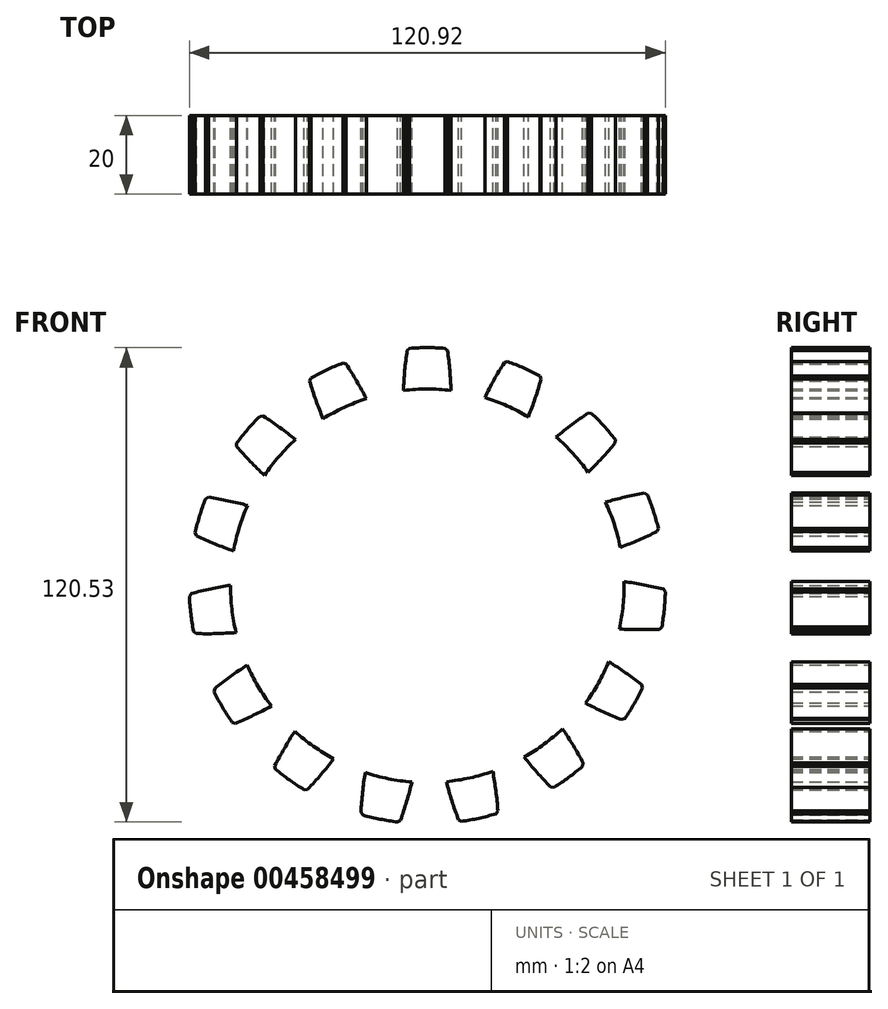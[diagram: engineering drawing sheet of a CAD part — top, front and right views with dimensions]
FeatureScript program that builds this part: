
annotation { "Feature Type Name" : "Feature", "Feature Type Description" : "" }
export const myFeature = defineFeature(function(context is Context, id is Id, definition is map)
    precondition{}
    {
        {
            var Q0;
            Q0=qCreatedBy(makeId("Front.planeOp"),FACE);
            var sketch = newSketch(context, id + "F0", { "sketchPlane" : qUnion([Q0])});
            skCircle(sketch, "E0", {"center": v(0, 0) * mm, "radius": 50 * mm});
            skArc(sketch, "E1", {"start": v(-2.05, -12.38) * mm, "mid": v(0, -12.55) * mm, "end": v(2.05, -12.38) * mm});
            skLineSegment(sketch, "E2.right", {"start": v(2.05, 10.3) * mm, "end": v(2.05, -12.38) * mm});
            skLineSegment(sketch, "E3.right", {"start": v(-2.05, 10.5) * mm, "end": v(-2.05, -12.38) * mm});
            skLineSegment(sketch, "E4", {"start": v(2.05, 10.3) * mm, "end": v(2.05, 12.38) * mm});
            skLineSegment(sketch, "E5", {"start": v(2.05, 12.38) * mm, "end": v(2.05, 10.3) * mm});
            skLineSegment(sketch, "E6", {"start": v(-2.05, 10.5) * mm, "end": v(-2.05, 12.38) * mm});
            skPoint(sketch, "E7.orphan", {"position": v(0, 10.5) * mm});
            skArc(sketch, "E8.trimOffspring", {"start": v(2.05, 12.38) * mm, "mid": v(0, 12.55) * mm, "end": v(-2.05, 12.38) * mm});
            skLineSegment(sketch, "E9.1.0", {"start": v(-7.83, 7.29) * mm, "end": v(5.62, -11.22) * mm});
            skLineSegment(sketch, "E9.1.1", {"start": v(-7.83, 7.29) * mm, "end": v(-8.94, 8.81) * mm});
            skArc(sketch, "E9.1.2", {"start": v(-5.62, 11.22) * mm, "mid": v(-7.38, 10.15) * mm, "end": v(-8.94, 8.81) * mm});
            skLineSegment(sketch, "E9.1.3", {"start": v(-4.4, 9.54) * mm, "end": v(8.94, -8.81) * mm});
            skLineSegment(sketch, "E9.1.4", {"start": v(-5.62, 11.22) * mm, "end": v(-4.4, 9.54) * mm});
            skArc(sketch, "E9.1.5", {"start": v(5.62, -11.22) * mm, "mid": v(7.38, -10.15) * mm, "end": v(8.94, -8.81) * mm});
            skLineSegment(sketch, "E9.2.0", {"start": v(-10.62, 1.3) * mm, "end": v(11.14, -5.78) * mm});
            skLineSegment(sketch, "E9.2.1", {"start": v(-10.62, 1.3) * mm, "end": v(-12.4, 1.88) * mm});
            skArc(sketch, "E9.2.2", {"start": v(-11.14, 5.78) * mm, "mid": v(-11.94, 3.88) * mm, "end": v(-12.4, 1.88) * mm});
            skLineSegment(sketch, "E9.2.3", {"start": v(-9.16, 5.13) * mm, "end": v(12.4, -1.88) * mm});
            skLineSegment(sketch, "E9.2.4", {"start": v(-11.14, 5.78) * mm, "end": v(-9.16, 5.13) * mm});
            skArc(sketch, "E9.2.5", {"start": v(11.14, -5.78) * mm, "mid": v(11.94, -3.88) * mm, "end": v(12.4, -1.88) * mm});
            skLineSegment(sketch, "E9.3.0", {"start": v(-9.35, -5.2) * mm, "end": v(12.4, 1.88) * mm});
            skLineSegment(sketch, "E9.3.1", {"start": v(-9.35, -5.2) * mm, "end": v(-11.14, -5.78) * mm});
            skArc(sketch, "E9.3.2", {"start": v(-12.4, -1.88) * mm, "mid": v(-11.94, -3.88) * mm, "end": v(-11.14, -5.78) * mm});
            skLineSegment(sketch, "E9.3.3", {"start": v(-10.43, -1.23) * mm, "end": v(11.14, 5.78) * mm});
            skLineSegment(sketch, "E9.3.4", {"start": v(-12.4, -1.88) * mm, "end": v(-10.43, -1.23) * mm});
            skArc(sketch, "E9.3.5", {"start": v(12.4, 1.88) * mm, "mid": v(11.94, 3.88) * mm, "end": v(11.14, 5.78) * mm});
            skLineSegment(sketch, "E9.4.0", {"start": v(-4.51, -9.7) * mm, "end": v(8.94, 8.81) * mm});
            skLineSegment(sketch, "E9.4.1", {"start": v(-4.51, -9.7) * mm, "end": v(-5.62, -11.22) * mm});
            skArc(sketch, "E9.4.2", {"start": v(-8.94, -8.81) * mm, "mid": v(-7.38, -10.15) * mm, "end": v(-5.62, -11.22) * mm});
            skLineSegment(sketch, "E9.4.3", {"start": v(-7.71, -7.13) * mm, "end": v(5.62, 11.22) * mm});
            skLineSegment(sketch, "E9.4.4", {"start": v(-8.94, -8.81) * mm, "end": v(-7.71, -7.13) * mm});
            skArc(sketch, "E9.4.5", {"start": v(8.94, 8.81) * mm, "mid": v(7.38, 10.15) * mm, "end": v(5.62, 11.22) * mm});
            skLineSegment(sketch, "E9.5.0", {"start": v(2.05, -10.5) * mm, "end": v(2.05, 12.38) * mm});
            skLineSegment(sketch, "E9.5.1", {"start": v(2.05, -10.5) * mm, "end": v(2.05, -12.38) * mm});
            skLineSegment(sketch, "E9.5.3", {"start": v(-2.05, -10.3) * mm, "end": v(-2.05, 12.38) * mm});
            skLineSegment(sketch, "E9.5.4", {"start": v(-2.05, -12.38) * mm, "end": v(-2.05, -10.3) * mm});
            skLineSegment(sketch, "E9.6.0", {"start": v(7.83, -7.29) * mm, "end": v(-5.62, 11.22) * mm});
            skLineSegment(sketch, "E9.6.1", {"start": v(7.83, -7.29) * mm, "end": v(8.94, -8.81) * mm});
            skArc(sketch, "E9.6.2", {"start": v(5.62, -11.22) * mm, "mid": v(7.38, -10.15) * mm, "end": v(8.94, -8.81) * mm});
            skLineSegment(sketch, "E9.6.3", {"start": v(4.4, -9.54) * mm, "end": v(-8.94, 8.81) * mm});
            skLineSegment(sketch, "E9.6.4", {"start": v(5.62, -11.22) * mm, "end": v(4.4, -9.54) * mm});
            skArc(sketch, "E9.6.5", {"start": v(-5.62, 11.22) * mm, "mid": v(-7.38, 10.15) * mm, "end": v(-8.94, 8.81) * mm});
            skLineSegment(sketch, "E9.7.0", {"start": v(10.62, -1.3) * mm, "end": v(-11.14, 5.78) * mm});
            skLineSegment(sketch, "E9.7.1", {"start": v(10.62, -1.3) * mm, "end": v(12.4, -1.88) * mm});
            skArc(sketch, "E9.7.2", {"start": v(11.14, -5.78) * mm, "mid": v(11.94, -3.88) * mm, "end": v(12.4, -1.88) * mm});
            skLineSegment(sketch, "E9.7.3", {"start": v(9.16, -5.13) * mm, "end": v(-12.4, 1.88) * mm});
            skLineSegment(sketch, "E9.7.4", {"start": v(11.14, -5.78) * mm, "end": v(9.16, -5.13) * mm});
            skArc(sketch, "E9.7.5", {"start": v(-11.14, 5.78) * mm, "mid": v(-11.94, 3.88) * mm, "end": v(-12.4, 1.88) * mm});
            skLineSegment(sketch, "E9.8.0", {"start": v(9.35, 5.2) * mm, "end": v(-12.4, -1.88) * mm});
            skLineSegment(sketch, "E9.8.1", {"start": v(9.35, 5.2) * mm, "end": v(11.14, 5.78) * mm});
            skArc(sketch, "E9.8.2", {"start": v(12.4, 1.88) * mm, "mid": v(11.94, 3.88) * mm, "end": v(11.14, 5.78) * mm});
            skLineSegment(sketch, "E9.8.3", {"start": v(10.43, 1.23) * mm, "end": v(-11.14, -5.78) * mm});
            skLineSegment(sketch, "E9.8.4", {"start": v(12.4, 1.88) * mm, "end": v(10.43, 1.23) * mm});
            skArc(sketch, "E9.8.5", {"start": v(-12.4, -1.88) * mm, "mid": v(-11.94, -3.88) * mm, "end": v(-11.14, -5.78) * mm});
            skLineSegment(sketch, "E9.9.0", {"start": v(4.51, 9.7) * mm, "end": v(-8.94, -8.81) * mm});
            skLineSegment(sketch, "E9.9.1", {"start": v(4.51, 9.7) * mm, "end": v(5.62, 11.22) * mm});
            skArc(sketch, "E9.9.2", {"start": v(8.94, 8.81) * mm, "mid": v(7.38, 10.15) * mm, "end": v(5.62, 11.22) * mm});
            skLineSegment(sketch, "E9.9.3", {"start": v(7.71, 7.13) * mm, "end": v(-5.62, -11.22) * mm});
            skLineSegment(sketch, "E9.9.4", {"start": v(8.94, 8.81) * mm, "end": v(7.71, 7.13) * mm});
            skArc(sketch, "E9.9.5", {"start": v(-8.94, -8.81) * mm, "mid": v(-7.38, -10.15) * mm, "end": v(-5.62, -11.22) * mm});
            skLineSegment(sketch, "E10", {"start": v(0, 50) * mm, "end": v(0, 46.5) * mm, "construction": true});
            skLineSegment(sketch, "E11", {"start": v(0, 46.5) * mm, "end": v(83.9, 46.5) * mm, "construction": true});
            skArc(sketch, "E12", {"start": v(-5.04, 60.29) * mm, "mid": v(-5.7, 54.98) * mm, "end": v(-6.05, 49.63) * mm});
            skArc(sketch, "E13", {"start": v(5.04, 60.29) * mm, "mid": v(0, 60.5) * mm, "end": v(-5.04, 60.29) * mm});
            skArc(sketch, "E14.MirrorC", {"start": v(5.04, 60.29) * mm, "mid": v(5.83, 53.42) * mm, "end": v(6.1, 46.5) * mm});
            skArc(sketch, "E15.trimOffspring", {"start": v(-6.8, 0.06) * mm, "mid": v(-6.85, -0.01) * mm, "end": v(-6.9, -0.08) * mm});
            skArc(sketch, "E16.trimOffspring", {"start": v(4.73, 3.7) * mm, "mid": v(4.84, 3.5) * mm, "end": v(4.94, 3.31) * mm});
            skArc(sketch, "E17.trimOffspring", {"start": v(6.8, 0.06) * mm, "mid": v(6.85, -0.01) * mm, "end": v(6.9, -0.08) * mm});
            skArc(sketch, "E18.1.0", {"start": v(29.06, 53.07) * mm, "mid": v(24.54, 55.3) * mm, "end": v(19.85, 57.15) * mm});
            skArc(sketch, "E18.1.1", {"start": v(19.85, 57.15) * mm, "mid": v(17.09, 52.56) * mm, "end": v(14.6, 47.82) * mm});
            skArc(sketch, "E18.1.2", {"start": v(29.06, 53.07) * mm, "mid": v(27, 46.46) * mm, "end": v(24.44, 40.03) * mm});
            skArc(sketch, "E18.2.0", {"start": v(48.08, 36.72) * mm, "mid": v(44.86, 40.6) * mm, "end": v(41.32, 44.19) * mm});
            skArc(sketch, "E18.2.1", {"start": v(41.32, 44.19) * mm, "mid": v(36.94, 41.11) * mm, "end": v(32.75, 37.79) * mm});
            skArc(sketch, "E18.2.2", {"start": v(48.08, 36.72) * mm, "mid": v(43.52, 31.52) * mm, "end": v(38.57, 26.68) * mm});
            skArc(sketch, "E18.3.0", {"start": v(58.84, 14.06) * mm, "mid": v(57.47, 18.91) * mm, "end": v(55.7, 23.63) * mm});
            skArc(sketch, "E18.3.1", {"start": v(55.7, 23.63) * mm, "mid": v(50.44, 22.6) * mm, "end": v(45.26, 21.26) * mm});
            skArc(sketch, "E18.3.2", {"start": v(58.84, 14.06) * mm, "mid": v(52.56, 11.15) * mm, "end": v(46.08, 8.74) * mm});
            skArc(sketch, "E18.4.0", {"start": v(59.49, -11.02) * mm, "mid": v(60.2, -6.02) * mm, "end": v(60.5, -1) * mm});
            skArc(sketch, "E18.4.1", {"start": v(60.5, -1) * mm, "mid": v(55.27, 0.2) * mm, "end": v(49.99, 1.07) * mm});
            skArc(sketch, "E18.4.2", {"start": v(59.49, -11.02) * mm, "mid": v(52.57, -11.12) * mm, "end": v(45.66, -10.7) * mm});
            skArc(sketch, "E18.5.0", {"start": v(49.9, -34.2) * mm, "mid": v(52.58, -29.92) * mm, "end": v(54.9, -25.44) * mm});
            skArc(sketch, "E18.5.1", {"start": v(54.9, -25.44) * mm, "mid": v(50.6, -22.24) * mm, "end": v(46.13, -19.3) * mm});
            skArc(sketch, "E18.5.2", {"start": v(49.9, -34.2) * mm, "mid": v(43.54, -31.49) * mm, "end": v(37.4, -28.3) * mm});
            skArc(sketch, "E18.6.0", {"start": v(31.75, -51.5) * mm, "mid": v(35.93, -48.68) * mm, "end": v(39.85, -45.52) * mm});
            skArc(sketch, "E18.6.1", {"start": v(39.85, -45.52) * mm, "mid": v(37.23, -40.85) * mm, "end": v(34.34, -36.34) * mm});
            skArc(sketch, "E18.6.2", {"start": v(31.75, -51.5) * mm, "mid": v(27.03, -46.44) * mm, "end": v(22.7, -41.04) * mm});
            skArc(sketch, "E18.7.0", {"start": v(8.13, -59.95) * mm, "mid": v(13.1, -59.07) * mm, "end": v(17.97, -57.77) * mm});
            skArc(sketch, "E18.7.1", {"start": v(17.97, -57.77) * mm, "mid": v(17.46, -52.44) * mm, "end": v(16.64, -47.15) * mm});
            skArc(sketch, "E18.7.2", {"start": v(8.13, -59.95) * mm, "mid": v(5.87, -53.41) * mm, "end": v(4.1, -46.72) * mm});
            skArc(sketch, "E18.8.0", {"start": v(-16.88, -58.1) * mm, "mid": v(-11.99, -59.3) * mm, "end": v(-7, -60.1) * mm});
            skArc(sketch, "E18.8.1", {"start": v(-7, -60.1) * mm, "mid": v(-5.3, -55.02) * mm, "end": v(-3.9, -49.85) * mm});
            skArc(sketch, "E18.8.2", {"start": v(-16.88, -58.1) * mm, "mid": v(-16.3, -51.2) * mm, "end": v(-15.2, -44.37) * mm});
            skArc(sketch, "E18.9.0", {"start": v(-39, -46.26) * mm, "mid": v(-35, -49.34) * mm, "end": v(-30.78, -52.09) * mm});
            skArc(sketch, "E18.9.1", {"start": v(-30.78, -52.09) * mm, "mid": v(-27.16, -48.14) * mm, "end": v(-23.8, -43.98) * mm});
            skArc(sketch, "E18.9.2", {"start": v(-39, -46.26) * mm, "mid": v(-35.67, -40.19) * mm, "end": v(-31.88, -34.4) * mm});
            skArc(sketch, "E18.10.0", {"start": v(-54.4, -26.46) * mm, "mid": v(-52.01, -30.9) * mm, "end": v(-49.26, -35.12) * mm});
            skArc(sketch, "E18.10.1", {"start": v(-49.26, -35.12) * mm, "mid": v(-44.35, -32.98) * mm, "end": v(-39.58, -30.55) * mm});
            skArc(sketch, "E18.10.2", {"start": v(-54.4, -26.46) * mm, "mid": v(-48.9, -22.27) * mm, "end": v(-43.1, -18.5) * mm});
            skArc(sketch, "E18.11.0", {"start": v(-60.46, -2.12) * mm, "mid": v(-60.08, -7.15) * mm, "end": v(-59.27, -12.13) * mm});
            skArc(sketch, "E18.11.1", {"start": v(-59.27, -12.13) * mm, "mid": v(-53.92, -12.16) * mm, "end": v(-48.57, -11.87) * mm});
            skArc(sketch, "E18.11.2", {"start": v(-60.46, -2.12) * mm, "mid": v(-53.73, -0.52) * mm, "end": v(-46.9, 0.56) * mm});
            skArc(sketch, "E18.12.0", {"start": v(-56.13, 22.58) * mm, "mid": v(-57.81, 17.83) * mm, "end": v(-59.1, 12.96) * mm});
            skArc(sketch, "E18.12.1", {"start": v(-59.1, 12.96) * mm, "mid": v(-54.21, 10.76) * mm, "end": v(-49.21, 8.85) * mm});
            skArc(sketch, "E18.12.2", {"start": v(-56.13, 22.58) * mm, "mid": v(-49.32, 21.32) * mm, "end": v(-42.64, 19.54) * mm});
            skArc(sketch, "E18.13.0", {"start": v(-42.14, 43.4) * mm, "mid": v(-45.61, 39.75) * mm, "end": v(-48.76, 35.81) * mm});
            skArc(sketch, "E18.13.1", {"start": v(-48.76, 35.81) * mm, "mid": v(-45.2, 31.82) * mm, "end": v(-41.39, 28.05) * mm});
            skArc(sketch, "E18.13.2", {"start": v(-42.14, 43.4) * mm, "mid": v(-36.44, 39.5) * mm, "end": v(-31.05, 35.15) * mm});
            skArc(sketch, "E18.14.0", {"start": v(-20.91, 56.77) * mm, "mid": v(-25.57, 54.83) * mm, "end": v(-30.04, 52.51) * mm});
            skArc(sketch, "E18.14.1", {"start": v(-30.04, 52.51) * mm, "mid": v(-28.4, 47.42) * mm, "end": v(-26.45, 42.43) * mm});
            skArc(sketch, "E18.14.2", {"start": v(-20.91, 56.77) * mm, "mid": v(-17.29, 50.88) * mm, "end": v(-14.12, 44.72) * mm});
            skLineSegment(sketch, "E18.anchor1", {"start": v(0, 0) * mm, "end": v(-5.04, 60.29) * mm, "construction": true});
            skLineSegment(sketch, "E18.anchor2", {"start": v(0, 0) * mm, "end": v(-30.04, 52.51) * mm, "construction": true});
            skCircle(sketch, "E19", {"center": v(0, 0) * mm, "radius": 10.5 * mm});
            skSolve(sketch);
        }
        {
            var Q0;
            {var subQ0=sQuery(id+"F0.wireOp",EDGE,"E12");Q0=makeQuery(id+"F0.imprint","IMPRINT",FACE,{"disambiguationData":[TD([[makeQuery(id+"F0.imprint","IMPRINT",EDGE,{"derivedFrom":subQ0}),1.0]])]});}
            var Q1;
            {var subQ4=sQuery(id+"F0.wireOp",EDGE,"E18.14.0");Q1=makeQuery(id+"F0.imprint","IMPRINT",FACE,{"disambiguationData":[TD([[makeQuery(id+"F0.imprint","IMPRINT",EDGE,{"derivedFrom":subQ4}),1.0]])]});}
            var Q2;
            {var subQ4=sQuery(id+"F0.wireOp",EDGE,"E18.13.0");Q2=makeQuery(id+"F0.imprint","IMPRINT",FACE,{"disambiguationData":[TD([[makeQuery(id+"F0.imprint","IMPRINT",EDGE,{"derivedFrom":subQ4}),1.0]])]});}
            var Q3;
            {var subQ4=sQuery(id+"F0.wireOp",EDGE,"E18.12.0");Q3=makeQuery(id+"F0.imprint","IMPRINT",FACE,{"disambiguationData":[TD([[makeQuery(id+"F0.imprint","IMPRINT",EDGE,{"derivedFrom":subQ4}),1.0]])]});}
            var Q4;
            {var subQ4=sQuery(id+"F0.wireOp",EDGE,"E18.11.0");Q4=makeQuery(id+"F0.imprint","IMPRINT",FACE,{"disambiguationData":[TD([[makeQuery(id+"F0.imprint","IMPRINT",EDGE,{"derivedFrom":subQ4}),1.0]])]});}
            var Q5;
            {var subQ4=sQuery(id+"F0.wireOp",EDGE,"E18.10.0");Q5=makeQuery(id+"F0.imprint","IMPRINT",FACE,{"disambiguationData":[TD([[makeQuery(id+"F0.imprint","IMPRINT",EDGE,{"derivedFrom":subQ4}),1.0]])]});}
            var Q6;
            {var subQ4=sQuery(id+"F0.wireOp",EDGE,"E18.9.0");Q6=makeQuery(id+"F0.imprint","IMPRINT",FACE,{"disambiguationData":[TD([[makeQuery(id+"F0.imprint","IMPRINT",EDGE,{"derivedFrom":subQ4}),1.0]])]});}
            var Q7;
            {var subQ4=sQuery(id+"F0.wireOp",EDGE,"E18.8.0");Q7=makeQuery(id+"F0.imprint","IMPRINT",FACE,{"disambiguationData":[TD([[makeQuery(id+"F0.imprint","IMPRINT",EDGE,{"derivedFrom":subQ4}),1.0]])]});}
            var Q8;
            {var subQ4=sQuery(id+"F0.wireOp",EDGE,"E18.7.0");Q8=makeQuery(id+"F0.imprint","IMPRINT",FACE,{"disambiguationData":[TD([[makeQuery(id+"F0.imprint","IMPRINT",EDGE,{"derivedFrom":subQ4}),1.0]])]});}
            var Q9;
            {var subQ4=sQuery(id+"F0.wireOp",EDGE,"E18.5.0");Q9=makeQuery(id+"F0.imprint","IMPRINT",FACE,{"disambiguationData":[TD([[makeQuery(id+"F0.imprint","IMPRINT",EDGE,{"derivedFrom":subQ4}),1.0]])]});}
            var Q10;
            {var subQ4=sQuery(id+"F0.wireOp",EDGE,"E18.4.0");Q10=makeQuery(id+"F0.imprint","IMPRINT",FACE,{"disambiguationData":[TD([[makeQuery(id+"F0.imprint","IMPRINT",EDGE,{"derivedFrom":subQ4}),1.0]])]});}
            var Q11;
            {var subQ4=sQuery(id+"F0.wireOp",EDGE,"E18.3.0");Q11=makeQuery(id+"F0.imprint","IMPRINT",FACE,{"disambiguationData":[TD([[makeQuery(id+"F0.imprint","IMPRINT",EDGE,{"derivedFrom":subQ4}),1.0]])]});}
            var Q12;
            {var subQ4=sQuery(id+"F0.wireOp",EDGE,"E18.2.0");Q12=makeQuery(id+"F0.imprint","IMPRINT",FACE,{"disambiguationData":[TD([[makeQuery(id+"F0.imprint","IMPRINT",EDGE,{"derivedFrom":subQ4}),1.0]])]});}
            var Q13;
            {var subQ4=sQuery(id+"F0.wireOp",EDGE,"E18.1.0");Q13=makeQuery(id+"F0.imprint","IMPRINT",FACE,{"disambiguationData":[TD([[makeQuery(id+"F0.imprint","IMPRINT",EDGE,{"derivedFrom":subQ4}),1.0]])]});}
            var Q14;
            {var subQ4=sQuery(id+"F0.wireOp",EDGE,"E18.6.0");Q14=makeQuery(id+"F0.imprint","IMPRINT",FACE,{"disambiguationData":[TD([[makeQuery(id+"F0.imprint","IMPRINT",EDGE,{"derivedFrom":subQ4}),1.0]])]});}
            var Q15;
            {var subQ8=sQuery(id+"F0.wireOp",EDGE,"E9.5.1");Q15=makeQuery(id+"F0.imprint","IMPRINT",FACE,{"disambiguationData":[TD([[makeQuery(id+"F0.imprint","IMPRINT",EDGE,{"derivedFrom":subQ8}),1.0]])]});}
            extrude(context, id + "F1", {"entities" : qUnion([Q0, Q1, Q2, Q3, Q4, Q5, Q6, Q7, Q8, Q9, Q10, Q11, Q12, Q13, Q14, Q15]), "depth" : 20 * mm});
        }
        {
            var Q0;
            Q0=makeQuery(id+"F1.opExtrude","SWEPT_EDGE",EDGE,{"disambiguationData":[OSD([sQuery(id+"F0.wireOp",EDGE,"E12"),sQuery(id+"F0.wireOp",EDGE,"E13")])]});
            var Q1;
            Q1=makeQuery(id+"F1.opExtrude","SWEPT_EDGE",EDGE,{"disambiguationData":[OSD([sQuery(id+"F0.wireOp",EDGE,"E13"),sQuery(id+"F0.wireOp",EDGE,"E14.MirrorC")])]});
            var Q2;
            Q2=makeQuery(id+"F1.opExtrude","SWEPT_EDGE",EDGE,{"disambiguationData":[OSD([sQuery(id+"F0.wireOp",EDGE,"E18.14.0"),sQuery(id+"F0.wireOp",EDGE,"E18.14.2")])]});
            var Q3;
            Q3=makeQuery(id+"F1.opExtrude","SWEPT_EDGE",EDGE,{"disambiguationData":[OSD([sQuery(id+"F0.wireOp",EDGE,"E18.14.0"),sQuery(id+"F0.wireOp",EDGE,"E18.14.1")])]});
            var Q4;
            Q4=makeQuery(id+"F1.opExtrude","SWEPT_EDGE",EDGE,{"disambiguationData":[OSD([sQuery(id+"F0.wireOp",EDGE,"E18.13.0"),sQuery(id+"F0.wireOp",EDGE,"E18.13.2")])]});
            var Q5;
            Q5=makeQuery(id+"F1.opExtrude","SWEPT_EDGE",EDGE,{"disambiguationData":[OSD([sQuery(id+"F0.wireOp",EDGE,"E18.13.0"),sQuery(id+"F0.wireOp",EDGE,"E18.13.1")])]});
            var Q6;
            Q6=makeQuery(id+"F1.opExtrude","SWEPT_EDGE",EDGE,{"disambiguationData":[OSD([sQuery(id+"F0.wireOp",EDGE,"E18.12.0"),sQuery(id+"F0.wireOp",EDGE,"E18.12.2")])]});
            var Q7;
            Q7=makeQuery(id+"F1.opExtrude","SWEPT_EDGE",EDGE,{"disambiguationData":[OSD([sQuery(id+"F0.wireOp",EDGE,"E18.12.0"),sQuery(id+"F0.wireOp",EDGE,"E18.12.1")])]});
            var Q8;
            Q8=makeQuery(id+"F1.opExtrude","SWEPT_EDGE",EDGE,{"disambiguationData":[OSD([sQuery(id+"F0.wireOp",EDGE,"E18.1.0"),sQuery(id+"F0.wireOp",EDGE,"E18.1.1")])]});
            var Q9;
            Q9=makeQuery(id+"F1.opExtrude","SWEPT_EDGE",EDGE,{"disambiguationData":[OSD([sQuery(id+"F0.wireOp",EDGE,"E18.1.0"),sQuery(id+"F0.wireOp",EDGE,"E18.1.2")])]});
            var Q10;
            Q10=makeQuery(id+"F1.opExtrude","SWEPT_EDGE",EDGE,{"disambiguationData":[OSD([sQuery(id+"F0.wireOp",EDGE,"E18.2.0"),sQuery(id+"F0.wireOp",EDGE,"E18.2.1")])]});
            var Q11;
            Q11=makeQuery(id+"F1.opExtrude","SWEPT_EDGE",EDGE,{"disambiguationData":[OSD([sQuery(id+"F0.wireOp",EDGE,"E18.2.0"),sQuery(id+"F0.wireOp",EDGE,"E18.2.2")])]});
            var Q12;
            Q12=makeQuery(id+"F1.opExtrude","SWEPT_EDGE",EDGE,{"disambiguationData":[OSD([sQuery(id+"F0.wireOp",EDGE,"E18.3.0"),sQuery(id+"F0.wireOp",EDGE,"E18.3.1")])]});
            var Q13;
            Q13=makeQuery(id+"F1.opExtrude","SWEPT_EDGE",EDGE,{"disambiguationData":[OSD([sQuery(id+"F0.wireOp",EDGE,"E18.3.0"),sQuery(id+"F0.wireOp",EDGE,"E18.3.2")])]});
            var Q14;
            Q14=makeQuery(id+"F1.opExtrude","SWEPT_EDGE",EDGE,{"disambiguationData":[OSD([sQuery(id+"F0.wireOp",EDGE,"E18.4.0"),sQuery(id+"F0.wireOp",EDGE,"E18.4.1")])]});
            var Q15;
            Q15=makeQuery(id+"F1.opExtrude","SWEPT_EDGE",EDGE,{"disambiguationData":[OSD([sQuery(id+"F0.wireOp",EDGE,"E18.4.0"),sQuery(id+"F0.wireOp",EDGE,"E18.4.2")])]});
            var Q16;
            Q16=makeQuery(id+"F1.opExtrude","SWEPT_EDGE",EDGE,{"disambiguationData":[OSD([sQuery(id+"F0.wireOp",EDGE,"E18.5.0"),sQuery(id+"F0.wireOp",EDGE,"E18.5.1")])]});
            var Q17;
            Q17=makeQuery(id+"F1.opExtrude","SWEPT_EDGE",EDGE,{"disambiguationData":[OSD([sQuery(id+"F0.wireOp",EDGE,"E18.5.0"),sQuery(id+"F0.wireOp",EDGE,"E18.5.2")])]});
            var Q18;
            Q18=makeQuery(id+"F1.opExtrude","SWEPT_EDGE",EDGE,{"disambiguationData":[OSD([sQuery(id+"F0.wireOp",EDGE,"E18.6.0"),sQuery(id+"F0.wireOp",EDGE,"E18.6.1")])]});
            var Q19;
            Q19=makeQuery(id+"F1.opExtrude","SWEPT_EDGE",EDGE,{"disambiguationData":[OSD([sQuery(id+"F0.wireOp",EDGE,"E18.6.0"),sQuery(id+"F0.wireOp",EDGE,"E18.6.2")])]});
            var Q20;
            Q20=makeQuery(id+"F1.opExtrude","SWEPT_EDGE",EDGE,{"disambiguationData":[OSD([sQuery(id+"F0.wireOp",EDGE,"E18.7.0"),sQuery(id+"F0.wireOp",EDGE,"E18.7.1")])]});
            var Q21;
            Q21=makeQuery(id+"F1.opExtrude","SWEPT_EDGE",EDGE,{"disambiguationData":[OSD([sQuery(id+"F0.wireOp",EDGE,"E18.7.0"),sQuery(id+"F0.wireOp",EDGE,"E18.7.2")])]});
            var Q22;
            Q22=makeQuery(id+"F1.opExtrude","SWEPT_EDGE",EDGE,{"disambiguationData":[OSD([sQuery(id+"F0.wireOp",EDGE,"E18.8.0"),sQuery(id+"F0.wireOp",EDGE,"E18.8.1")])]});
            var Q23;
            Q23=makeQuery(id+"F1.opExtrude","SWEPT_EDGE",EDGE,{"disambiguationData":[OSD([sQuery(id+"F0.wireOp",EDGE,"E18.8.0"),sQuery(id+"F0.wireOp",EDGE,"E18.8.2")])]});
            var Q24;
            Q24=makeQuery(id+"F1.opExtrude","SWEPT_EDGE",EDGE,{"disambiguationData":[OSD([sQuery(id+"F0.wireOp",EDGE,"E18.11.0"),sQuery(id+"F0.wireOp",EDGE,"E18.11.2")])]});
            var Q25;
            Q25=makeQuery(id+"F1.opExtrude","SWEPT_EDGE",EDGE,{"disambiguationData":[OSD([sQuery(id+"F0.wireOp",EDGE,"E18.11.0"),sQuery(id+"F0.wireOp",EDGE,"E18.11.1")])]});
            var Q26;
            Q26=makeQuery(id+"F1.opExtrude","SWEPT_EDGE",EDGE,{"disambiguationData":[OSD([sQuery(id+"F0.wireOp",EDGE,"E18.10.0"),sQuery(id+"F0.wireOp",EDGE,"E18.10.2")])]});
            var Q27;
            Q27=makeQuery(id+"F1.opExtrude","SWEPT_EDGE",EDGE,{"disambiguationData":[OSD([sQuery(id+"F0.wireOp",EDGE,"E18.10.0"),sQuery(id+"F0.wireOp",EDGE,"E18.10.1")])]});
            var Q28;
            Q28=makeQuery(id+"F1.opExtrude","SWEPT_EDGE",EDGE,{"disambiguationData":[OSD([sQuery(id+"F0.wireOp",EDGE,"E18.9.0"),sQuery(id+"F0.wireOp",EDGE,"E18.9.2")])]});
            var Q29;
            Q29=makeQuery(id+"F1.opExtrude","SWEPT_EDGE",EDGE,{"disambiguationData":[OSD([sQuery(id+"F0.wireOp",EDGE,"E18.9.0"),sQuery(id+"F0.wireOp",EDGE,"E18.9.1")])]});
            chamfer(context, id + "F2", {"entities" : qUnion([Q0, Q1, Q2, Q3, Q4, Q5, Q6, Q7, Q8, Q9, Q10, Q11, Q12, Q13, Q14, Q15, Q16, Q17, Q18, Q19, Q20, Q21, Q22, Q23, Q24, Q25, Q26, Q27, Q28, Q29]), "width" : 0.7 * mm, "tangentPropagation" : true});
        }
    });
